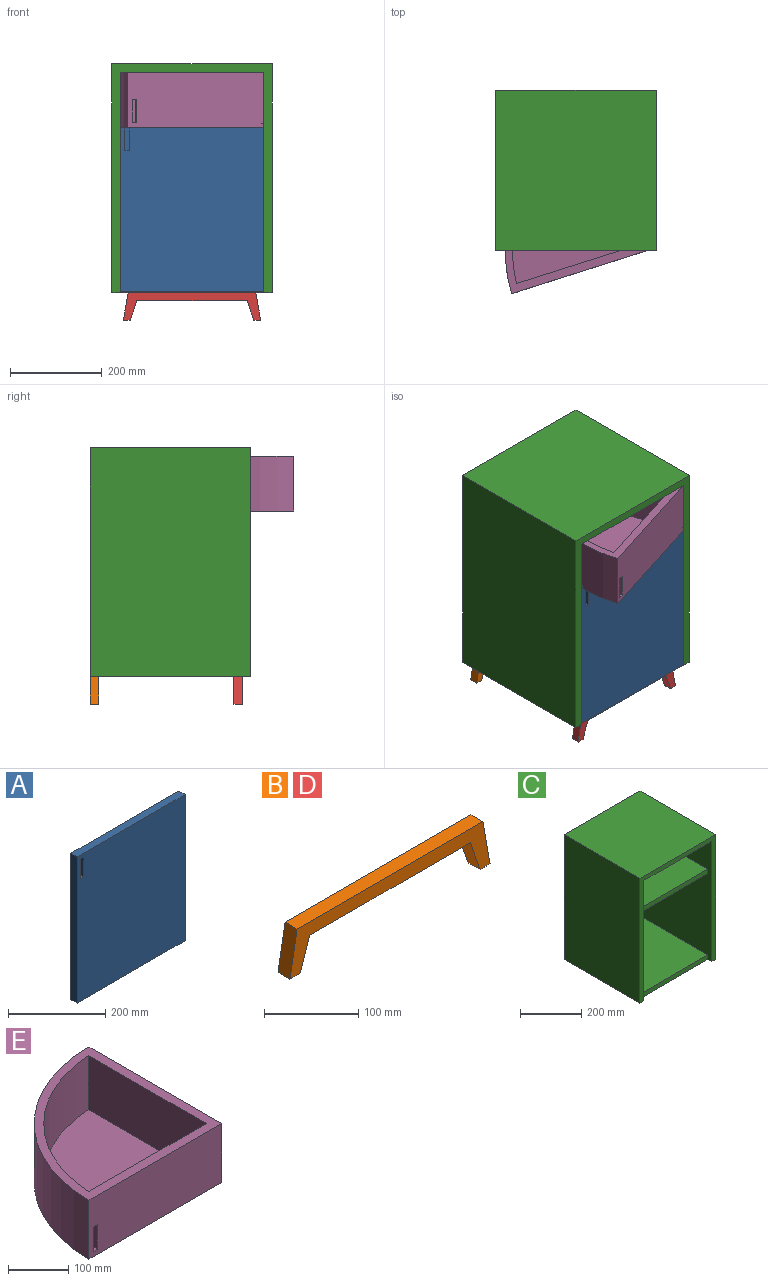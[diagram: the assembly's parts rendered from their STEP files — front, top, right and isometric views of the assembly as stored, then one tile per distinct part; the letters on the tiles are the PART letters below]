
ASSEMBLY  parts=5 mates=4
PART A: 11 faces, bbox 314x18x368 mm
  f0: plane 368x314mm, normal (0,-1,0), area 115052mm2, adj f1,f2,f3,f4,f6,f7,f8,f9
  f1: plane 314x18mm, normal (0,0,-1), area 5652mm2, adj f0,f2,f4,f5
  f2: plane 368x18mm, normal (1,0,0), area 6624mm2, adj f0,f1,f3,f5
  f3: plane 314x18mm, normal (0,0,1), area 5652mm2, adj f0,f2,f4,f5
  f4: plane 368x18mm, normal (-1,0,0), area 6624mm2, adj f0,f1,f3,f5
  f5: plane 368x314mm, normal (0,1,0), area 115552mm2, adj f1,f2,f3,f4
  f6: plane 10x10mm, normal (0,0,-1), area 100mm2, adj f0,f7,f9,f10
  f7: plane 50x10mm, normal (1,0,0), area 500mm2, adj f0,f6,f8,f10
  f8: plane 10x10mm, normal (0,0,1), area 100mm2, adj f0,f7,f9,f10
  f9: plane 50x10mm, normal (-1,0,0), area 500mm2, adj f0,f6,f8,f10
  f10: plane 50x10mm, normal (0,-1,0), area 500mm2, adj f6,f7,f8,f9
PART B: 10 faces, bbox 300x18x60 mm
  f0: plane 18x15mm, normal (0,0,-1), area 270mm2, adj f3,f4,f6,f8
  f1: plane 18x15mm, normal (0,0,-1), area 270mm2, adj f3,f4,f5,f9
  f2: plane 278.84x18mm, normal (0,0,1), area 5019.1mm2, adj f3,f4,f5,f6
  f3: plane 300x60mm, normal (0,-1,0), area 6562.4mm2, adj f0,f1,f2,f5,f6,f7,f8,f9
  f4: plane 300x60mm, normal (0,1,0), area 6562.4mm2, adj f0,f1,f2,f5,f6,f7,f8,f9
  f5: plane 60x18mm, normal (0.98,0,0.17), area 1096.7mm2, adj f1,f2,f3,f4
  f6: plane 60x18mm, normal (-0.98,0,0.17), area 1096.7mm2, adj f0,f2,f3,f4
  f7: plane 241.09x18mm, normal (0,0,-1), area 4339.7mm2, adj f3,f4,f8,f9
  f8: plane 42.27x18mm, normal (0.95,0,-0.32), area 804.2mm2, adj f0,f3,f4,f7
  f9: plane 42.27x18mm, normal (-0.95,0,-0.32), area 804.2mm2, adj f1,f3,f4,f7
PART C: 16 faces, bbox 350x350x500 mm
  f0: plane 350x350mm, normal (0,0,-1), area 116848mm2, adj f1,f3,f4,f5,f6,f8,f15
  f1: plane 500x350mm, normal (1,0,0), area 175000mm2, adj f0,f2,f4,f5
  f2: plane 350x350mm, normal (0,0,1), area 122500mm2, adj f1,f3,f4,f5
  f3: plane 500x350mm, normal (-1,0,0), area 175000mm2, adj f0,f2,f4,f5
  f4: plane 500x350mm, normal (0,-1,0), area 23652mm2, adj f0,f1,f2,f3,f6,f8,f9
  f5: plane 500x350mm, normal (0,1,0), area 175000mm2, adj f0,f1,f2,f3
  f6: plane 482x330mm, normal (1,0,0), area 147828mm2, adj f0,f4,f7,f9,f10,f11,f12,f13
  f7: plane 314x312mm, normal (0,0,1), area 97968mm2, adj f6,f8,f10,f11
  f8: plane 482x330mm, normal (-1,0,0), area 147828mm2, adj f0,f4,f7,f9,f10,f11,f12,f13
  f9: plane 330x314mm, normal (0,0,-1), area 103620mm2, adj f4,f6,f8,f10
  f10: plane 314x120mm, normal (0,-1,0), area 37680mm2, adj f6,f7,f8,f9
  f11: plane 314x18mm, normal (0,-1,0), area 5652mm2, adj f6,f7,f8,f12
  f12: plane 314x312mm, normal (0,0,-1), area 97968mm2, adj f6,f8,f11,f14
  f13: plane 314x312mm, normal (0,0,1), area 97968mm2, adj f6,f8,f14,f15
  f14: plane 326x314mm, normal (0,-1,0), area 102364mm2, adj f6,f8,f12,f13
  f15: plane 314x18mm, normal (0,-1,0), area 5652mm2, adj f0,f6,f8,f13
PART D: same geometry as B
PART E: 14 faces, bbox 312x312x120 mm
  f0: plane 312x120mm, normal (0,-1,0), area 36940mm2, adj f1,f2,f3,f4,f9,f10,f11,f12
  f1: plane 312x120mm, normal (1,0,0), area 37440mm2, adj f0,f2,f3,f4
  f2: cylinder r=312mm len=312mm, axis (0,0,-1), area 58810.6mm2, adj f0,f1,f3,f4
  f3: plane 312x312mm, normal (0,0,1), area 17965.8mm2, adj f0,f1,f2,f5,f6,f7
  f4: plane 312x312mm, normal (0,0,-1), area 76453.8mm2, adj f0,f1,f2
  f5: cylinder r=296mm len=277.45mm, axis (0,0,1), area 47182.7mm2, adj f3,f6,f7,f8
  f6: plane 277.45x110mm, normal (0,1,0), area 30519.7mm2, adj f3,f5,f7,f8
  f7: plane 277.45x110mm, normal (-1,0,0), area 30519.7mm2, adj f3,f5,f6,f8
  f8: plane 277.45x277.45mm, normal (0,0,1), area 58488mm2, adj f5,f6,f7
  f9: plane 50x10mm, normal (1,0,0), area 500mm2, adj f0,f10,f12,f13
  f10: plane 10x10mm, normal (0,0,1), area 100mm2, adj f0,f9,f11,f13
  f11: plane 50x10mm, normal (-1,0,0), area 500mm2, adj f0,f10,f12,f13
  f12: plane 10x10mm, normal (0,0,-1), area 100mm2, adj f0,f9,f11,f13
  f13: plane 50x10mm, normal (0,-1,0), area 500mm2, adj f9,f10,f11,f12
PLACE A rot(axis=(-0.53,0.04,0.85),0deg) t=(-85.43,-365.28,-14.98)mm
PLACE B t=(-92.43,-33.28,-76.98)mm
PLACE C t=(-67.43,-33.28,-16.98)mm
PLACE D t=(-92.43,-347.28,-76.98)mm
PLACE E rot(axis=(0,0,1),17.6deg) t=(-85.43,-383.28,345.02)mm
MATE fastened C.f0 <-> B.f2  axis (0,0,-1) through (-242.43,-33.28,-16.98)mm
MATE fastened D.f2 <-> C.f0  axis (0,0,1) through (-242.43,-365.28,-16.98)mm
MATE fastened A.f2 <-> C.f8  axis (1,0,0) through (-85.43,-383.28,169.02)mm
MATE revolute E.f2 <-> C.f9  axis (0,0,1) through (-85.43,-383.28,465.02)mm
